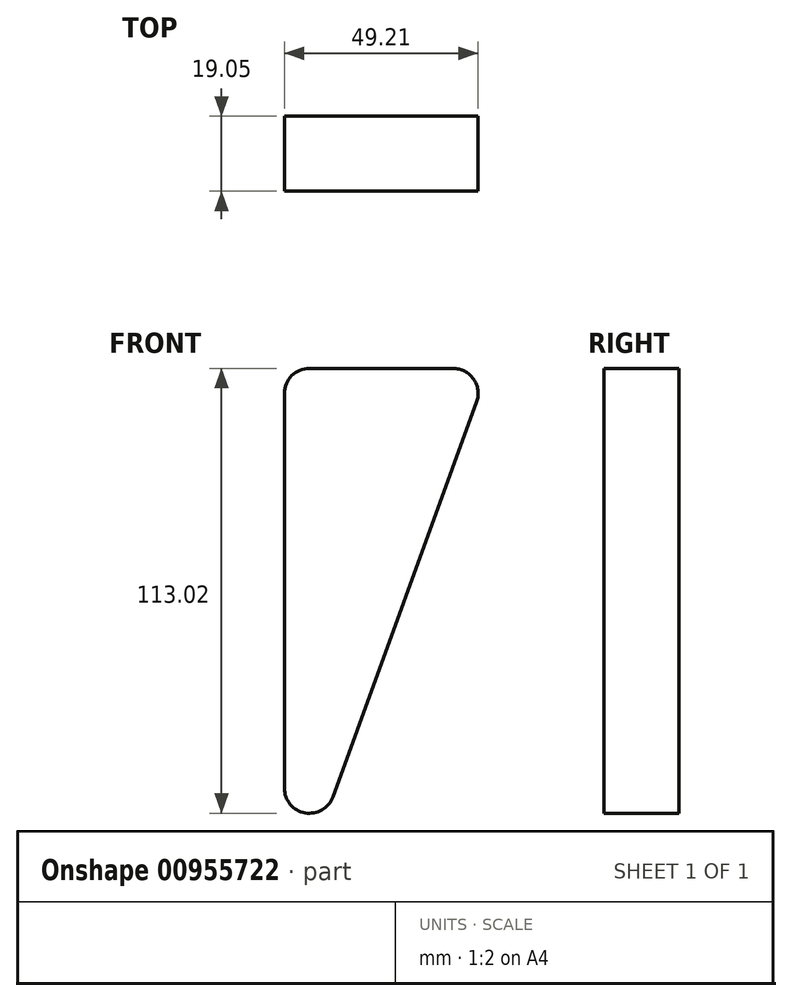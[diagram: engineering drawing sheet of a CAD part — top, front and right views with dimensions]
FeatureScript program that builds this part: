
annotation { "Feature Type Name" : "Feature", "Feature Type Description" : "" }
export const myFeature = defineFeature(function(context is Context, id is Id, definition is map)
    precondition{}
    {
        {
            var Q0;
            Q0=qCreatedBy(makeId("Front.planeOp"),FACE);
            var sketch = newSketch(context, id + "F0", { "sketchPlane" : qUnion([Q0])});
            skLineSegment(sketch, "E0", {"start": v(0, 0) * mm, "end": v(0, 518.57) * mm, "construction": true});
            skLineSegment(sketch, "E1", {"start": v(-127, 0) * mm, "end": v(-177.8, 0) * mm});
            skLineSegment(sketch, "E2", {"start": v(-9.53, 482.6) * mm, "end": v(-114.43, 482.6) * mm});
            skLineSegment(sketch, "E3", {"start": v(-114.43, 482.6) * mm, "end": v(-114.43, 508) * mm});
            skLineSegment(sketch, "E4", {"start": v(-114.43, 508) * mm, "end": v(-152.53, 508) * mm});
            skLineSegment(sketch, "E5", {"start": v(-152.53, 508) * mm, "end": v(-152.53, 482.6) * mm});
            skLineSegment(sketch, "E6", {"start": v(-152.53, 482.6) * mm, "end": v(-76.2, 272.9) * mm});
            skFitSpline(sketch, "E7", {"points": [v(-177.8, 0) * mm, v(-76.2, 272.9) * mm], "startDerivative": vector(-14.26, 190.8) * mm, "endDerivative": vector(298.2, 231.03) * mm});
            skFitSpline(sketch, "E8", {"points": [v(-127, 0) * mm, v(0, 177.8) * mm], "startDerivative": vector(15.82, 238.53) * mm, "endDerivative": vector(279.75, 55.19) * mm});
            skLineSegment(sketch, "E9.MirrorCS", {"start": v(114.43, 508) * mm, "end": v(152.53, 508) * mm});
            skLineSegment(sketch, "E10.MirrorCS", {"start": v(152.53, 508) * mm, "end": v(152.53, 482.6) * mm});
            skLineSegment(sketch, "E11.MirrorCS", {"start": v(114.43, 482.6) * mm, "end": v(114.43, 508) * mm});
            skLineSegment(sketch, "E12.MirrorCS", {"start": v(127, 0) * mm, "end": v(177.8, 0) * mm});
            skFitSpline(sketch, "E13.MirrorCS", {"points": [v(177.8, 0) * mm, v(76.2, 272.9) * mm], "startDerivative": vector(14.26, 190.8) * mm, "endDerivative": vector(-298.2, 231.03) * mm});
            skLineSegment(sketch, "E14.MirrorCS", {"start": v(152.53, 482.6) * mm, "end": v(76.2, 272.9) * mm});
            skFitSpline(sketch, "E15.MirrorCS", {"points": [v(127, 0) * mm, v(0, 177.8) * mm], "startDerivative": vector(-15.82, 238.53) * mm, "endDerivative": vector(-279.75, 55.19) * mm});
            skLineSegment(sketch, "E16.MirrorCS", {"start": v(9.53, 482.6) * mm, "end": v(114.43, 482.6) * mm});
            skLineSegment(sketch, "E17", {"start": v(-9.53, 482.6) * mm, "end": v(9.53, 482.6) * mm});
            skLineSegment(sketch, "E18.top", {"start": v(-9.53, 330.2) * mm, "end": v(9.52, 330.2) * mm});
            skLineSegment(sketch, "E18.left", {"start": v(-9.53, 175.65) * mm, "end": v(-9.53, 330.2) * mm});
            skLineSegment(sketch, "E18.right", {"start": v(9.52, 175.65) * mm, "end": v(9.53, 330.2) * mm});
            skSolve(sketch);
        }
        {
            var Q0;
            Q0=makeQuery(id+"F0.imprint","IMPRINT",FACE,{"disambiguationData":[TD([[makeQuery(id+"F0.imprint","IMPRINT",EDGE,{"derivedFrom":sQuery(id+"F0.wireOp",EDGE,"E1")}),-1.0]])]});
            extrude(context, id + "F1", {"entities" : qUnion([Q0]), "depth" : 19.05 * mm, "offsetDistance" : 25.4 * mm});
        }
        {
            var Q0;
            Q0=makeQuery(id+"F1.opExtrude","CAP_FACE",FACE,{"disambiguationData":[OSD([sQuery(id+"F0.wireOp",EDGE,"E1"),sQuery(id+"F0.wireOp",EDGE,"0hf62t5t-19fe-gNLj-W87e-903Vq9vZiqhL"),sQuery(id+"F0.wireOp",EDGE,"qQeWkWD5-kGTr-0nGU-dVlZ-qIkPo3TVKBMq"),sQuery(id+"F0.wireOp",EDGE,"E2"),sQuery(id+"F0.wireOp",EDGE,"E3"),sQuery(id+"F0.wireOp",EDGE,"E4"),sQuery(id+"F0.wireOp",EDGE,"E5"),sQuery(id+"F0.wireOp",EDGE,"E6"),sQuery(id+"F0.wireOp",EDGE,"E7"),sQuery(id+"F0.wireOp",EDGE,"E8"),sQuery(id+"F0.wireOp",EDGE,"E10.MirrorCS"),sQuery(id+"F0.wireOp",EDGE,"E12.MirrorCS"),sQuery(id+"F0.wireOp",EDGE,"E13.MirrorCS"),sQuery(id+"F0.wireOp",EDGE,"E14.MirrorCS"),sQuery(id+"F0.wireOp",EDGE,"E15.MirrorCS"),sQuery(id+"F0.wireOp",EDGE,"E16.MirrorCS"),sQuery(id+"F0.wireOp",EDGE,"E11.MirrorCS"),sQuery(id+"F0.wireOp",EDGE,"E9.MirrorCS"),sQuery(id+"F0.wireOp",EDGE,"93ac58f0-caf0-4c1f-ac85-953fb1b0919e0.MirrorCS"),sQuery(id+"F0.wireOp",EDGE,"f764d514-46c8-48c8-bec5-b047bbb404510.MirrorCS")])],"isStart":false});
            var sketch = newSketch(context, id + "F2", { "sketchPlane" : qUnion([Q0])});
            skLineSegment(sketch, "E19.0", {"start": v(-104.08, 442.33) * mm, "end": v(-67.57, 342) * mm});
            skLineSegment(sketch, "E20.0", {"start": v(-61.6, 450.85) * mm, "end": v(-98.11, 450.85) * mm});
            skLineSegment(sketch, "E21.0", {"start": v(-55.25, 344.18) * mm, "end": v(-55.25, 444.5) * mm});
            skPoint(sketch, "E22.visualSharp", {"position": v(-55.25, 450.85) * mm});
            skArc(sketch, "E22.filletArc", {"start": v(-55.25, 444.5) * mm, "mid": v(-57.1, 449) * mm, "end": v(-61.6, 450.85) * mm});
            skPoint(sketch, "E23.visualSharp", {"position": v(-107.18, 450.85) * mm});
            skArc(sketch, "E23.filletArc", {"start": v(-98.11, 450.85) * mm, "mid": v(-103.32, 448.14) * mm, "end": v(-104.08, 442.33) * mm});
            skPoint(sketch, "E24.visualSharp", {"position": v(-55.25, 308.16) * mm});
            skArc(sketch, "E24.filletArc", {"start": v(-67.57, 342) * mm, "mid": v(-60.5, 337.92) * mm, "end": v(-55.25, 344.18) * mm});
            skArc(sketch, "E25.MirrorCS", {"start": v(55.25, 444.5) * mm, "mid": v(57.1, 449) * mm, "end": v(61.6, 450.85) * mm});
            skArc(sketch, "E26.MirrorCS", {"start": v(98.11, 450.85) * mm, "mid": v(103.32, 448.14) * mm, "end": v(104.08, 442.33) * mm});
            skArc(sketch, "E27.MirrorCS", {"start": v(67.57, 342) * mm, "mid": v(60.5, 337.92) * mm, "end": v(55.25, 344.18) * mm});
            skPoint(sketch, "E28.MirrorP", {"position": v(55.25, 450.85) * mm});
            skPoint(sketch, "E29.MirrorP", {"position": v(107.18, 450.85) * mm});
            skPoint(sketch, "E30.MirrorP", {"position": v(55.25, 308.16) * mm});
            skLineSegment(sketch, "E31.MirrorCS", {"start": v(104.08, 442.33) * mm, "end": v(67.57, 342) * mm});
            skLineSegment(sketch, "E32.MirrorCS", {"start": v(55.25, 344.18) * mm, "end": v(55.25, 444.5) * mm});
            skLineSegment(sketch, "E33.MirrorCS", {"start": v(61.6, 450.85) * mm, "end": v(98.11, 450.85) * mm});
            skSolve(sketch);
        }
        {
            var Q0;
            Q0=makeQuery(id+"F2.imprint","IMPRINT",FACE,{"disambiguationData":[TD([[makeQuery(id+"F2.imprint","IMPRINT",EDGE,{"derivedFrom":sQuery(id+"F2.wireOp",EDGE,"E19.0")}),1.0]])]});
            var Q1;
            Q1=makeQuery(id+"F2.imprint","IMPRINT",FACE,{"disambiguationData":[TD([[makeQuery(id+"F2.imprint","IMPRINT",EDGE,{"derivedFrom":sQuery(id+"F2.wireOp",EDGE,"E25.MirrorCS")}),-1.0]])]});
            extrude(context, id + "F3", {"entities" : qUnion([Q0, Q1]), "operationType" : NewBodyOperationType.REMOVE, "oppositeDirection" : true, "depth" : 25.4 * mm, "offsetDistance" : 25.4 * mm});
        }
    });
